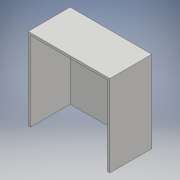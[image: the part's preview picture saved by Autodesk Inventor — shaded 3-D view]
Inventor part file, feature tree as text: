
AUTODESK INVENTOR PART (.ipt)
format: ipt  version: 2018 (Build 220112000, 112)  size: 114,176 bytes
history: native  units: mm
features: extrude x4, sketch x4, other x1
ambient origin geometry x8: Origin, YZ Plane, XZ Plane, XY Plane, X Axis, Y Axis, Z Axis, Center Point
bodies: Body1 (feature_tree)
feature tree (9):
  other  "ソリッド1"
  extrude  "押し出し1"  Depth=700.0mm
  extrude  "押し出し2"  Depth=700.0mm
  extrude  "押し出し3"  Depth=20.0mm TaperAngle=0.0deg
  extrude  "押し出し4"  Depth=700.0mm
  sketch  "スケッチ1"
  sketch  "スケッチ2"
  sketch  "スケッチ3"
  sketch  "スケッチ4"
